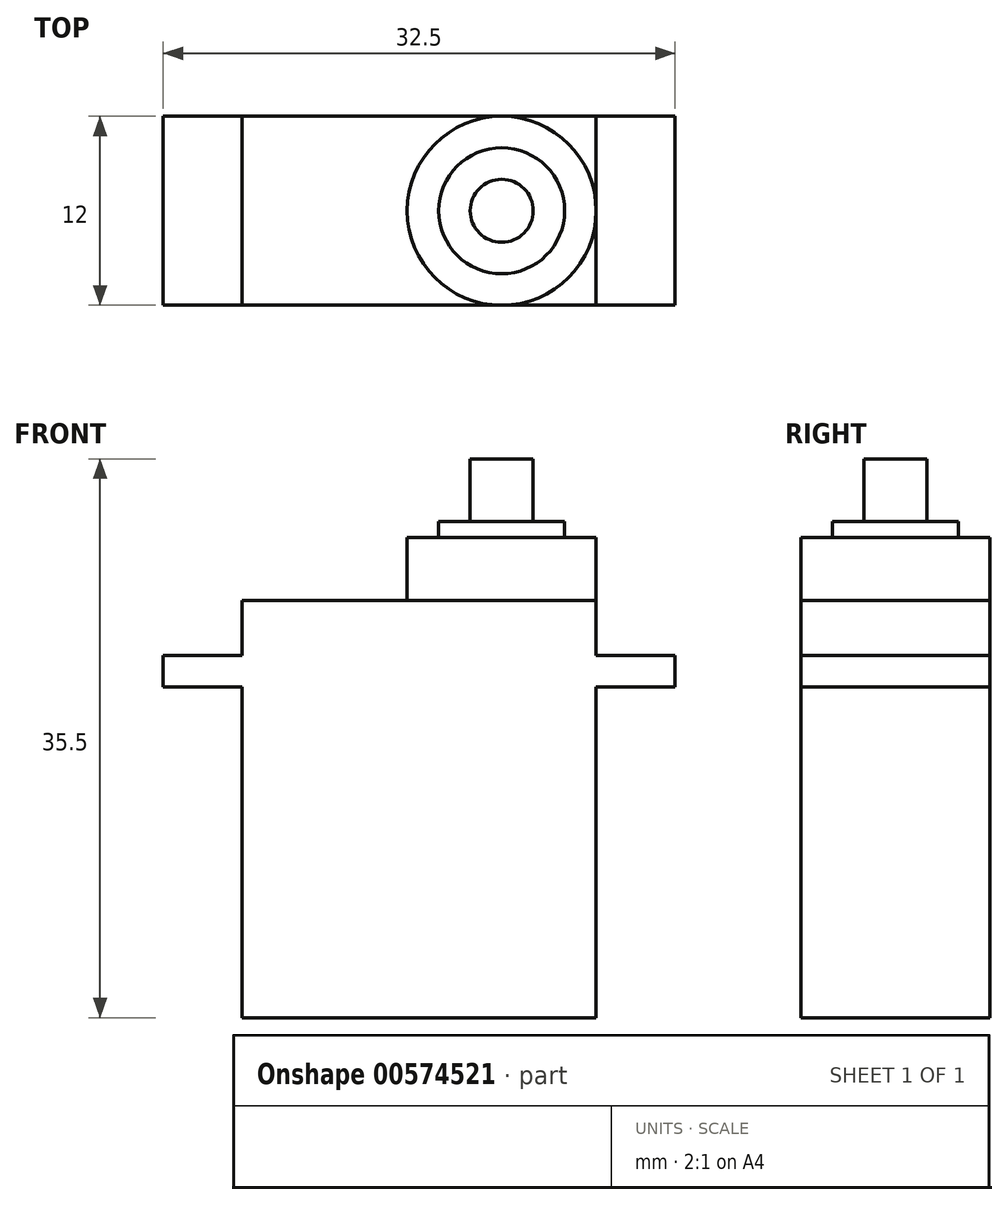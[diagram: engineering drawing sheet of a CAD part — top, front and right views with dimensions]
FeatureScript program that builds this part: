
annotation { "Feature Type Name" : "Feature", "Feature Type Description" : "" }
export const myFeature = defineFeature(function(context is Context, id is Id, definition is map)
    precondition{}
    {
        {
            var Q0;
            Q0=qCreatedBy(makeId("Top.planeOp"),FACE);
            var sketch = newSketch(context, id + "F0", { "sketchPlane" : qUnion([Q0])});
            skLineSegment(sketch, "E0.bottom", {"start": v(11.25, -6) * mm, "end": v(-11.25, -6) * mm});
            skLineSegment(sketch, "E0.top", {"start": v(11.25, 6) * mm, "end": v(-11.25, 6) * mm});
            skLineSegment(sketch, "E0.left", {"start": v(11.25, -6) * mm, "end": v(11.25, 6) * mm});
            skLineSegment(sketch, "E0.right", {"start": v(-11.25, -6) * mm, "end": v(-11.25, 6) * mm});
            skPoint(sketch, "E0.middle", {"position": v(0, 0) * mm});
            skSolve(sketch);
        }
        {
            var Q0;
            Q0=makeQuery(id+"F0.imprint","IMPRINT",FACE,{"disambiguationData":[TD([[makeQuery(id+"F0.imprint","IMPRINT",EDGE,{"derivedFrom":sQuery(id+"F0.wireOp",EDGE,"E0.bottom")}),-1.0]])]});
            extrude(context, id + "F1", {"entities" : qUnion([Q0]), "depth" : 21 * mm, "offsetDistance" : 25 * mm});
        }
        {
            var Q0;
            Q0=makeQuery(id+"F1.opExtrude","CAP_FACE",FACE,{"disambiguationData":[OSD([sQuery(id+"F0.wireOp",EDGE,"E0.bottom"),sQuery(id+"F0.wireOp",EDGE,"E0.top"),sQuery(id+"F0.wireOp",EDGE,"E0.left"),sQuery(id+"F0.wireOp",EDGE,"E0.right")])],"isStart":false});
            var sketch = newSketch(context, id + "F2", { "sketchPlane" : qUnion([Q0])});
            skLineSegment(sketch, "E1.bottom", {"start": v(-16.25, 6) * mm, "end": v(16.25, 6) * mm});
            skLineSegment(sketch, "E1.top", {"start": v(-16.25, -6) * mm, "end": v(16.25, -6) * mm});
            skLineSegment(sketch, "E1.left", {"start": v(-16.25, 6) * mm, "end": v(-16.25, -6) * mm});
            skLineSegment(sketch, "E1.right", {"start": v(16.25, 6) * mm, "end": v(16.25, -6) * mm});
            skPoint(sketch, "E1.middle", {"position": v(0, 0) * mm});
            skCircle(sketch, "E2", {"center": v(5.25, 0) * mm, "radius": 6 * mm});
            skPoint(sketch, "E2.centerSnap0", {"position": v(11.25, 0) * mm});
            skCircle(sketch, "E3", {"center": v(5.25, 0) * mm, "radius": 4 * mm});
            skCircle(sketch, "E4", {"center": v(5.25, 0) * mm, "radius": 2 * mm});
            skSolve(sketch);
        }
        {
            var Q0;
            {var subQ0=sQuery(id+"F2.wireOp",EDGE,"E1.bottom");var subQ3=sQuery(id+"F2.wireOp",EDGE,"E2");var subQ4=makeQuery(id+"F2.imprint","INTERSECT",VERTEX,{"derivedFrom":[subQ0,subQ3]});Q0=makeQuery(id+"F2.imprint","IMPRINT",FACE,{"disambiguationData":[TD([[makeQuery(id+"F2.imprint","IMPRINT",EDGE,{"disambiguationData":[TD([[subQ4,1.0]])],"derivedFrom":subQ0}),1.0]])]});}
            var Q1;
            {var subQ2=sQuery(id+"F2.wireOp",EDGE,"E1.left");Q1=makeQuery(id+"F2.imprint","IMPRINT",FACE,{"disambiguationData":[TD([[makeQuery(id+"F2.imprint","IMPRINT",EDGE,{"derivedFrom":subQ2}),1.0]])]});}
            var Q2;
            {var subQ0=sQuery(id+"F2.wireOp",EDGE,"E1.right");Q2=makeQuery(id+"F2.imprint","IMPRINT",FACE,{"disambiguationData":[TD([[makeQuery(id+"F2.imprint","IMPRINT",EDGE,{"derivedFrom":subQ0}),-1.0]])]});}
            var Q3;
            {var subQ0=sQuery(id+"F2.wireOp",EDGE,"E1.top");var subQ3=sQuery(id+"F2.wireOp",EDGE,"E2");var subQ4=makeQuery(id+"F2.imprint","INTERSECT",VERTEX,{"derivedFrom":[subQ0,subQ3]});Q3=makeQuery(id+"F2.imprint","IMPRINT",FACE,{"disambiguationData":[TD([[makeQuery(id+"F2.imprint","IMPRINT",EDGE,{"disambiguationData":[TD([[subQ4,1.0]])],"derivedFrom":subQ0}),-1.0]])]});}
            var Q4;
            Q4=makeQuery(id+"F2.imprint","IMPRINT",FACE,{"disambiguationData":[TD([[makeQuery(id+"F2.imprint","IMPRINT",EDGE,{"derivedFrom":sQuery(id+"F2.wireOp",EDGE,"E3")}),-1.0]])]});
            var Q5;
            Q5=makeQuery(id+"F2.imprint","IMPRINT",FACE,{"disambiguationData":[TD([[makeQuery(id+"F2.imprint","IMPRINT",EDGE,{"derivedFrom":sQuery(id+"F2.wireOp",EDGE,"E3")}),1.0]])]});
            var Q6;
            {var subQ1=makeQuery(id+"F1.opExtrude","CAP_EDGE",EDGE,{"disambiguationData":[OSD([sQuery(id+"F0.wireOp",EDGE,"E0.right")])],"isStart":false});Q6=makeQuery(id+"F2.imprint","IMPRINT",FACE,{"disambiguationData":[TD([[makeQuery(id+"F2.imprint","IMPRINT",EDGE,{"derivedFrom":subQ1}),-1.0]])]});}
            extrude(context, id + "F3", {"entities" : qUnion([Q0, Q1, Q2, Q3, Q4, Q5, Q6]), "operationType" : NewBodyOperationType.ADD, "depth" : 2 * mm, "offsetDistance" : 25 * mm});
        }
        {
            var Q0;
            Q0=makeQuery(id+"F2.imprint","IMPRINT",FACE,{"disambiguationData":[TD([[makeQuery(id+"F2.imprint","IMPRINT",EDGE,{"derivedFrom":sQuery(id+"F2.wireOp",EDGE,"E3")}),1.0]])]});
            var Q1;
            Q1=makeQuery(id+"F2.imprint","IMPRINT",FACE,{"disambiguationData":[TD([[makeQuery(id+"F2.imprint","IMPRINT",EDGE,{"derivedFrom":sQuery(id+"F2.wireOp",EDGE,"E3")}),-1.0]])]});
            var Q2;
            {var subQ1=makeQuery(id+"F1.opExtrude","CAP_EDGE",EDGE,{"disambiguationData":[OSD([sQuery(id+"F0.wireOp",EDGE,"E0.right")])],"isStart":false});Q2=makeQuery(id+"F2.imprint","IMPRINT",FACE,{"disambiguationData":[TD([[makeQuery(id+"F2.imprint","IMPRINT",EDGE,{"derivedFrom":subQ1}),-1.0]])]});}
            var Q3;
            {var subQ0=sQuery(id+"F2.wireOp",EDGE,"E1.top");var subQ3=sQuery(id+"F2.wireOp",EDGE,"E2");var subQ4=makeQuery(id+"F2.imprint","INTERSECT",VERTEX,{"derivedFrom":[subQ0,subQ3]});Q3=makeQuery(id+"F2.imprint","IMPRINT",FACE,{"disambiguationData":[TD([[makeQuery(id+"F2.imprint","IMPRINT",EDGE,{"disambiguationData":[TD([[subQ4,1.0]])],"derivedFrom":subQ0}),-1.0]])]});}
            var Q4;
            {var subQ0=sQuery(id+"F2.wireOp",EDGE,"E1.bottom");var subQ3=sQuery(id+"F2.wireOp",EDGE,"E2");var subQ4=makeQuery(id+"F2.imprint","INTERSECT",VERTEX,{"derivedFrom":[subQ0,subQ3]});Q4=makeQuery(id+"F2.imprint","IMPRINT",FACE,{"disambiguationData":[TD([[makeQuery(id+"F2.imprint","IMPRINT",EDGE,{"disambiguationData":[TD([[subQ4,1.0]])],"derivedFrom":subQ0}),1.0]])]});}
            extrude(context, id + "F4", {"entities" : qUnion([Q0, Q1, Q2, Q3, Q4]), "operationType" : NewBodyOperationType.ADD, "depth" : 5.5 * mm, "offsetDistance" : 25 * mm});
        }
        {
            var Q0;
            Q0=makeQuery(id+"F2.imprint","IMPRINT",FACE,{"disambiguationData":[TD([[makeQuery(id+"F2.imprint","IMPRINT",EDGE,{"derivedFrom":sQuery(id+"F2.wireOp",EDGE,"E3")}),1.0]])]});
            var Q1;
            Q1=makeQuery(id+"F2.imprint","IMPRINT",FACE,{"disambiguationData":[TD([[makeQuery(id+"F2.imprint","IMPRINT",EDGE,{"derivedFrom":sQuery(id+"F2.wireOp",EDGE,"E3")}),-1.0]])]});
            extrude(context, id + "F5", {"entities" : qUnion([Q0, Q1]), "operationType" : NewBodyOperationType.ADD, "depth" : 9.5 * mm, "offsetDistance" : 25 * mm});
        }
        {
            var Q0;
            Q0=makeQuery(id+"F2.imprint","IMPRINT",FACE,{"disambiguationData":[TD([[makeQuery(id+"F2.imprint","IMPRINT",EDGE,{"derivedFrom":sQuery(id+"F2.wireOp",EDGE,"E3")}),1.0]])]});
            extrude(context, id + "F6", {"entities" : qUnion([Q0]), "operationType" : NewBodyOperationType.ADD, "depth" : 10.5 * mm, "offsetDistance" : 25 * mm});
        }
        {
            var Q0;
            Q0=makeQuery(id+"F2.imprint","IMPRINT",FACE,{"disambiguationData":[TD([[makeQuery(id+"F2.imprint","IMPRINT",EDGE,{"derivedFrom":sQuery(id+"F2.wireOp",EDGE,"E4")}),1.0]])]});
            extrude(context, id + "F7", {"entities" : qUnion([Q0]), "operationType" : NewBodyOperationType.ADD, "depth" : 14.5 * mm, "offsetDistance" : 25 * mm});
        }
    });
